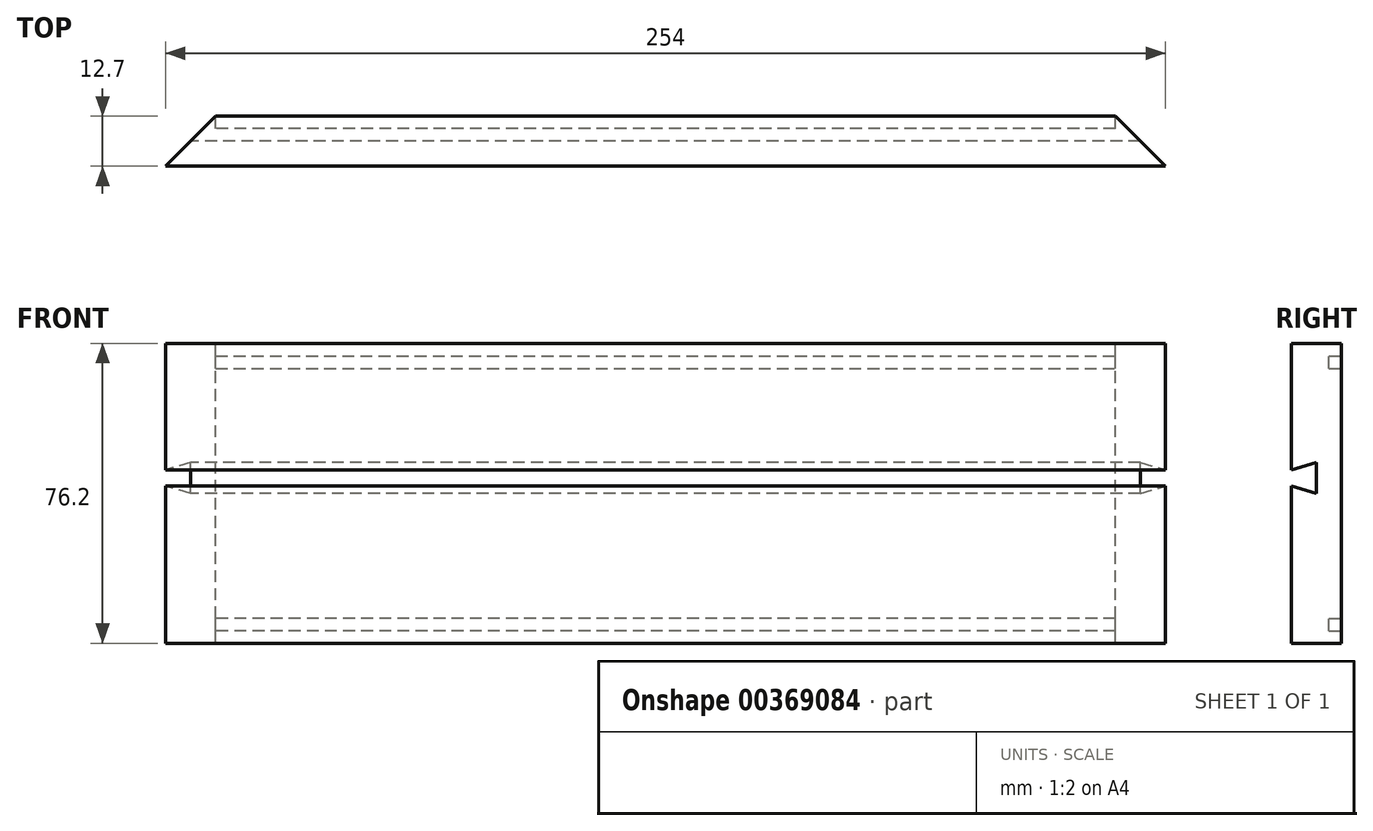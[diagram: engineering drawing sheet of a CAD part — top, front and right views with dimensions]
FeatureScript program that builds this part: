
annotation { "Feature Type Name" : "Feature", "Feature Type Description" : "" }
export const myFeature = defineFeature(function(context is Context, id is Id, definition is map)
    precondition{}
    {
        {
            var Q0;
            Q0=qCreatedBy(makeId("Front.planeOp"),FACE);
            var sketch = newSketch(context, id + "F0", { "sketchPlane" : qUnion([Q0])});
            skLineSegment(sketch, "E0.bottom", {"start": v(0, 0) * mm, "end": v(254, 0) * mm});
            skLineSegment(sketch, "E0.top", {"start": v(0, 76.2) * mm, "end": v(254, 76.2) * mm});
            skLineSegment(sketch, "E0.left", {"start": v(0, 0) * mm, "end": v(0, 76.2) * mm});
            skLineSegment(sketch, "E0.right", {"start": v(254, 0) * mm, "end": v(254, 76.2) * mm});
            skPoint(sketch, "E1.oppositeSnap0", {"position": v(0, 38.1) * mm});
            skLineSegment(sketch, "E1.bottom", {"start": v(0, 38.1) * mm, "end": v(-1.97, 38.1) * mm});
            skLineSegment(sketch, "E1.top", {"start": v(0, 38.1) * mm, "end": v(-1.97, 38.1) * mm});
            skLineSegment(sketch, "E1.left", {"start": v(0, 38.1) * mm, "end": v(0, 38.1) * mm});
            skLineSegment(sketch, "E1.right", {"start": v(-1.97, 38.1) * mm, "end": v(-1.97, 38.1) * mm});
            skSolve(sketch);
        }
        {
            var Q0;
            {var subQ3=sQuery(id+"F0.wireOp",EDGE,"E0.bottom");Q0=makeQuery(id+"F0.imprint","IMPRINT",FACE,{"disambiguationData":[TD([[makeQuery(id+"F0.imprint","IMPRINT",EDGE,{"derivedFrom":subQ3}),1.0]])]});}
            extrude(context, id + "F1", {"entities" : qUnion([Q0]), "endBound" : BoundingType.SYMMETRIC, "depth" : 12.7 * mm});
        }
        {
            var Q0;
            Q0=makeQuery(id+"F1.opExtrude","SWEPT_FACE",FACE,{"disambiguationData":[OSD([sQuery(id+"F0.wireOp",EDGE,"E0.left")])]});
            var sketch = newSketch(context, id + "F2", { "sketchPlane" : qUnion([Q0])});
            skLineSegment(sketch, "E2", {"start": v(0, 38.1) * mm, "end": v(0, 45.91) * mm});
            skLineSegment(sketch, "E3", {"start": v(0, 45.91) * mm, "end": v(6.35, 44.09) * mm, "construction": true});
            skLineSegment(sketch, "E4", {"start": v(6.35, 44.09) * mm, "end": v(6.35, 39.92) * mm});
            skLineSegment(sketch, "E5", {"start": v(0, 38.1) * mm, "end": v(6.35, 39.92) * mm});
            skPoint(sketch, "E6.orphan", {"position": v(6.35, 38.1) * mm});
            skPoint(sketch, "E7.end.orphan", {"position": v(-6.35, 38.1) * mm});
            skLineSegment(sketch, "E8", {"start": v(0, 45.91) * mm, "end": v(6.35, 44.09) * mm});
            skSolve(sketch);
        }
        {
            var Q0;
            Q0 = qSketchRegion(id + "F2", true);
            extrude(context, id + "F3", {"entities" : qUnion([Q0]), "operationType" : NewBodyOperationType.REMOVE, "oppositeDirection" : true, "depth" : 279.4 * mm});
        }
        {
            var Q0;
            Q0=makeQuery(id+"F1.opExtrude","SWEPT_FACE",FACE,{"disambiguationData":[OSD([sQuery(id+"F0.wireOp",EDGE,"E0.top")])]});
            var sketch = newSketch(context, id + "F4", { "sketchPlane" : qUnion([Q0])});
            skLineSegment(sketch, "E9", {"start": v(0, -6.35) * mm, "end": v(12.7, 6.35) * mm});
            skLineSegment(sketch, "E10", {"start": v(254, -6.35) * mm, "end": v(241.3, 6.35) * mm});
            skSolve(sketch);
        }
        {
            var Q0;
            Q0 = qSketchRegion(id + "F4", true);
            var Q1;
            {var subQ0=sQuery(id+"F4.wireOp",EDGE,"E9");Q1=makeQuery(id+"F4.imprint","IMPRINT",FACE,{"disambiguationData":[TD([[makeQuery(id+"F4.imprint","IMPRINT",EDGE,{"derivedFrom":subQ0}),1.0]])]});}
            var Q2;
            {var subQ0=sQuery(id+"F4.wireOp",EDGE,"E10");Q2=makeQuery(id+"F4.imprint","IMPRINT",FACE,{"disambiguationData":[TD([[makeQuery(id+"F4.imprint","IMPRINT",EDGE,{"derivedFrom":subQ0}),-1.0]])]});}
            extrude(context, id + "F5", {"entities" : qUnion([Q0, Q1, Q2]), "operationType" : NewBodyOperationType.REMOVE, "endBound" : BoundingType.UP_TO_NEXT, "oppositeDirection" : true, "depth" : 25.4 * mm});
        }
        {
            var Q0;
            Q0=makeQuery(id+"F1.opExtrude","CAP_FACE",FACE,{"disambiguationData":[OSD([sQuery(id+"F0.wireOp",EDGE,"E0.bottom"),sQuery(id+"F0.wireOp",EDGE,"E0.top"),sQuery(id+"F0.wireOp",EDGE,"E0.left"),sQuery(id+"F0.wireOp",EDGE,"E0.right")])],"isStart":true});
            var sketch = newSketch(context, id + "F6", { "sketchPlane" : qUnion([Q0])});
            skLineSegment(sketch, "E11", {"start": v(-266.78, 3.17) * mm, "end": v(-12.7, 3.18) * mm});
            skLineSegment(sketch, "E12.0", {"start": v(-266.6, 6.35) * mm, "end": v(-12.7, 6.35) * mm});
            skLineSegment(sketch, "E13", {"start": v(-12.7, 73.03) * mm, "end": v(-241.3, 73.02) * mm});
            skLineSegment(sketch, "E14.0", {"start": v(-12.7, 69.85) * mm, "end": v(-241.3, 69.85) * mm});
            skSolve(sketch);
        }
        {
            var Q0;
            Q0 = qSketchRegion(id + "F6", true);
            var Q1;
            {var subQ0=sQuery(id+"F6.wireOp",EDGE,"E13");Q1=makeQuery(id+"F6.imprint","IMPRINT",FACE,{"disambiguationData":[TD([[makeQuery(id+"F6.imprint","IMPRINT",EDGE,{"derivedFrom":subQ0}),1.0]])]});}
            var Q2;
            {var subQ0=sQuery(id+"F6.wireOp",EDGE,"E11");var subQ1=sQuery(id+"F0.wireOp",EDGE,"E0.top");var subQ2=makeQuery(id+"F5.boolean.opBoolean","COPY",EDGE,{"derivedFrom":makeQuery(id+"F5.opExtrude","SWEPT_EDGE",EDGE,{"disambiguationData":[OSD([subQ1,sQuery(id+"F4.wireOp",EDGE,"E9")])]})});var subQ3=makeQuery(id+"F6.imprint","INTERSECT",VERTEX,{"derivedFrom":[subQ2,subQ0]});Q2=makeQuery(id+"F6.imprint","IMPRINT",FACE,{"disambiguationData":[TD([[makeQuery(id+"F6.imprint","IMPRINT",EDGE,{"disambiguationData":[TD([[subQ3,1.0]])],"derivedFrom":subQ0}),1.0]])]});}
            extrude(context, id + "F7", {"entities" : qUnion([Q0, Q1, Q2]), "operationType" : NewBodyOperationType.REMOVE, "oppositeDirection" : true, "depth" : 3.17 * mm});
        }
        {
            var Q0;
            Q0=makeQuery(id+"F1.opExtrude","SWEPT_BODY",BODY,{"disambiguationData":[OSD([sQuery(id+"F0.wireOp",EDGE,"E0.bottom"),sQuery(id+"F0.wireOp",EDGE,"E0.top"),sQuery(id+"F0.wireOp",EDGE,"E0.left"),sQuery(id+"F0.wireOp",EDGE,"E0.right")])]});
            transform(context, id + "F8", {"entities" : qUnion([Q0]), "transformType" : TransformType.TRANSLATION_3D, "dx" : 0 * mm, "dy" : 0 * mm, "dz" : 0 * mm, "makeCopy" : true});
        }
    });
